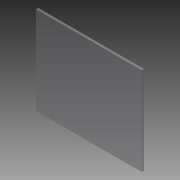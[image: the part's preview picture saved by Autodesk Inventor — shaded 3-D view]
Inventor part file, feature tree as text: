
AUTODESK INVENTOR PART (.ipt)
format: ipt  version: 2013 (Build 170138000, 138)  size: 67,072 bytes
history: native  units: in
note: dims shown in document units (in); Inventor stores cm internally (conversion verified against a paired STEP export)
features: extrude x1, sketch x1
ambient origin geometry x8: Origin, YZ Plane, XZ Plane, XY Plane, X Axis, Y Axis, Z Axis, Center Point
bodies: Solid1 (feature_tree)
feature tree (2):
  extrude  "Extrusion1"  Depth=6.0in
  sketch  "Sketch1"  dims[d0=5.0in d1=6.0in d2=0.125in d3=0.0in]
